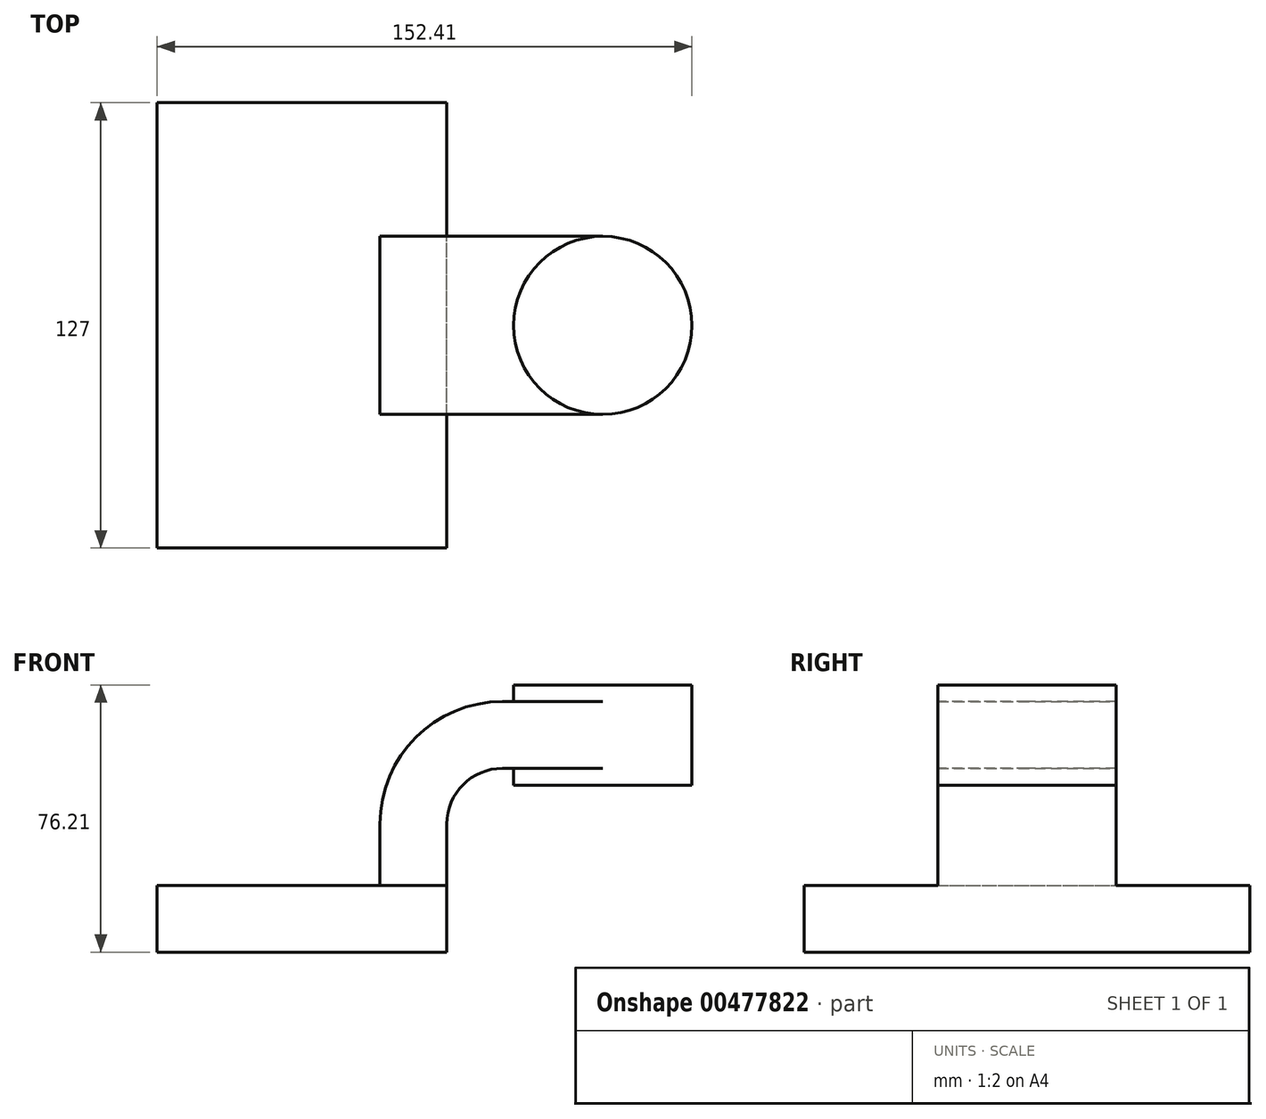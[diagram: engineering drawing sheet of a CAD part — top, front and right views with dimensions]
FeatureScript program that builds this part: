
annotation { "Feature Type Name" : "Feature", "Feature Type Description" : "" }
export const myFeature = defineFeature(function(context is Context, id is Id, definition is map)
    precondition{}
    {
        {
            var Q0;
            Q0=qCreatedBy(makeId("Front.planeOp"),FACE);
            var sketch = newSketch(context, id + "F0", { "sketchPlane" : qUnion([Q0])});
            skLineSegment(sketch, "E0.bottom", {"start": v(41.27, 9.53) * mm, "end": v(-41.28, 9.53) * mm});
            skLineSegment(sketch, "E0.top", {"start": v(41.28, -9.52) * mm, "end": v(-41.27, -9.52) * mm});
            skLineSegment(sketch, "E0.left", {"start": v(41.28, 9.53) * mm, "end": v(41.28, -9.52) * mm});
            skLineSegment(sketch, "E0.right", {"start": v(-41.28, 9.53) * mm, "end": v(-41.28, -9.52) * mm});
            skPoint(sketch, "E0.middle", {"position": v(0, 0) * mm});
            skLineSegment(sketch, "E1.bottom", {"start": v(111.12, 66.68) * mm, "end": v(60.33, 66.68) * mm});
            skLineSegment(sketch, "E1.top", {"start": v(111.12, 38.1) * mm, "end": v(60.33, 38.1) * mm});
            skLineSegment(sketch, "E1.left", {"start": v(111.12, 66.68) * mm, "end": v(111.12, 38.1) * mm});
            skLineSegment(sketch, "E1.right", {"start": v(60.33, 66.68) * mm, "end": v(60.33, 38.1) * mm});
            skPoint(sketch, "E1.middle", {"position": v(85.72, 52.39) * mm});
            skLineSegment(sketch, "E2", {"start": v(41.27, 9.53) * mm, "end": v(41.27, 27) * mm});
            skArc(sketch, "E3", {"start": v(41.27, 27) * mm, "mid": v(45.92, 38.23) * mm, "end": v(57.15, 42.88) * mm});
            skLineSegment(sketch, "E4", {"start": v(57.15, 42.88) * mm, "end": v(85.72, 42.88) * mm});
            skLineSegment(sketch, "E5.0", {"start": v(57.15, 61.93) * mm, "end": v(85.72, 61.93) * mm});
            skArc(sketch, "E5.1", {"start": v(22.22, 27) * mm, "mid": v(32.45, 51.7) * mm, "end": v(57.15, 61.93) * mm});
            skLineSegment(sketch, "E5.2", {"start": v(22.22, 9.53) * mm, "end": v(22.22, 27) * mm});
            skFitSpline(sketch, "E6", {"points": [v(-41.28, 9.53) * mm, v(57.15, 61.93) * mm], "startDerivative": vector(0.8, 83.66) * mm, "endDerivative": vector(140.77, -0.11) * mm});
            skLineSegment(sketch, "E7", {"start": v(85.72, 38.1) * mm, "end": v(85.72, 66.68) * mm});
            skLineSegment(sketch, "E8", {"start": v(85.72, 66.68) * mm, "end": v(111.12, 66.68) * mm});
            skSolve(sketch);
        }
        {
            var Q0;
            Q0=makeQuery(id+"F0.imprint","IMPRINT",FACE,{"disambiguationData":[TD([[makeQuery(id+"F0.imprint","IMPRINT",EDGE,{"derivedFrom":sQuery(id+"F0.wireOp",EDGE,"E0.top")}),-1.0]])]});
            extrude(context, id + "F1", {"entities" : qUnion([Q0]), "endBound" : BoundingType.SYMMETRIC, "depth" : 127 * mm});
        }
        {
            var Q0;
            {var subQ1=sQuery(id+"F0.wireOp",EDGE,"E2");Q0=makeQuery(id+"F0.imprint","IMPRINT",FACE,{"disambiguationData":[TD([[makeQuery(id+"F0.imprint","IMPRINT",EDGE,{"derivedFrom":subQ1}),1.0]])]});}
            var Q1;
            {var subQ0=sQuery(id+"F0.wireOp",EDGE,"E5.0");var subQ1=sQuery(id+"F0.wireOp",EDGE,"E1.right");var subQ2=makeQuery(id+"F0.imprint","INTERSECT",VERTEX,{"derivedFrom":[subQ1,subQ0]});Q1=makeQuery(id+"F0.imprint","IMPRINT",FACE,{"disambiguationData":[TD([[makeQuery(id+"F0.imprint","IMPRINT",EDGE,{"disambiguationData":[TD([[subQ2,-1.0]])],"derivedFrom":subQ1}),1.0]])]});}
            extrude(context, id + "F2", {"entities" : qUnion([Q0, Q1]), "operationType" : NewBodyOperationType.ADD, "endBound" : BoundingType.SYMMETRIC, "depth" : 50.8 * mm});
        }
        {
            var Q0;
            Q0=makeQuery(id+"F0.imprint","IMPRINT",FACE,{"disambiguationData":[TD([[makeQuery(id+"F0.imprint","IMPRINT",EDGE,{"derivedFrom":sQuery(id+"F0.wireOp",EDGE,"E5.1")}),1.0]])]});
            extrude(context, id + "F3", {"entities" : qUnion([Q0]), "operationType" : NewBodyOperationType.ADD, "depth" : 15.88 * mm});
        }
        {
            var Q0;
            {var subQ3=sQuery(id+"F0.wireOp",EDGE,"E1.left");Q0=makeQuery(id+"F0.imprint","IMPRINT",FACE,{"disambiguationData":[TD([[makeQuery(id+"F0.imprint","IMPRINT",EDGE,{"derivedFrom":subQ3}),-1.0]])]});}
            var Q1;
            Q1=sQuery(id+"F0.wireOp",EDGE,"E7");
            revolve(context, id + "F4", {"operationType" : NewBodyOperationType.ADD, "entities" : qUnion([Q0]), "axis" : qUnion([Q1]), "revolveType" : RevolveType.FULL});
        }
    });
